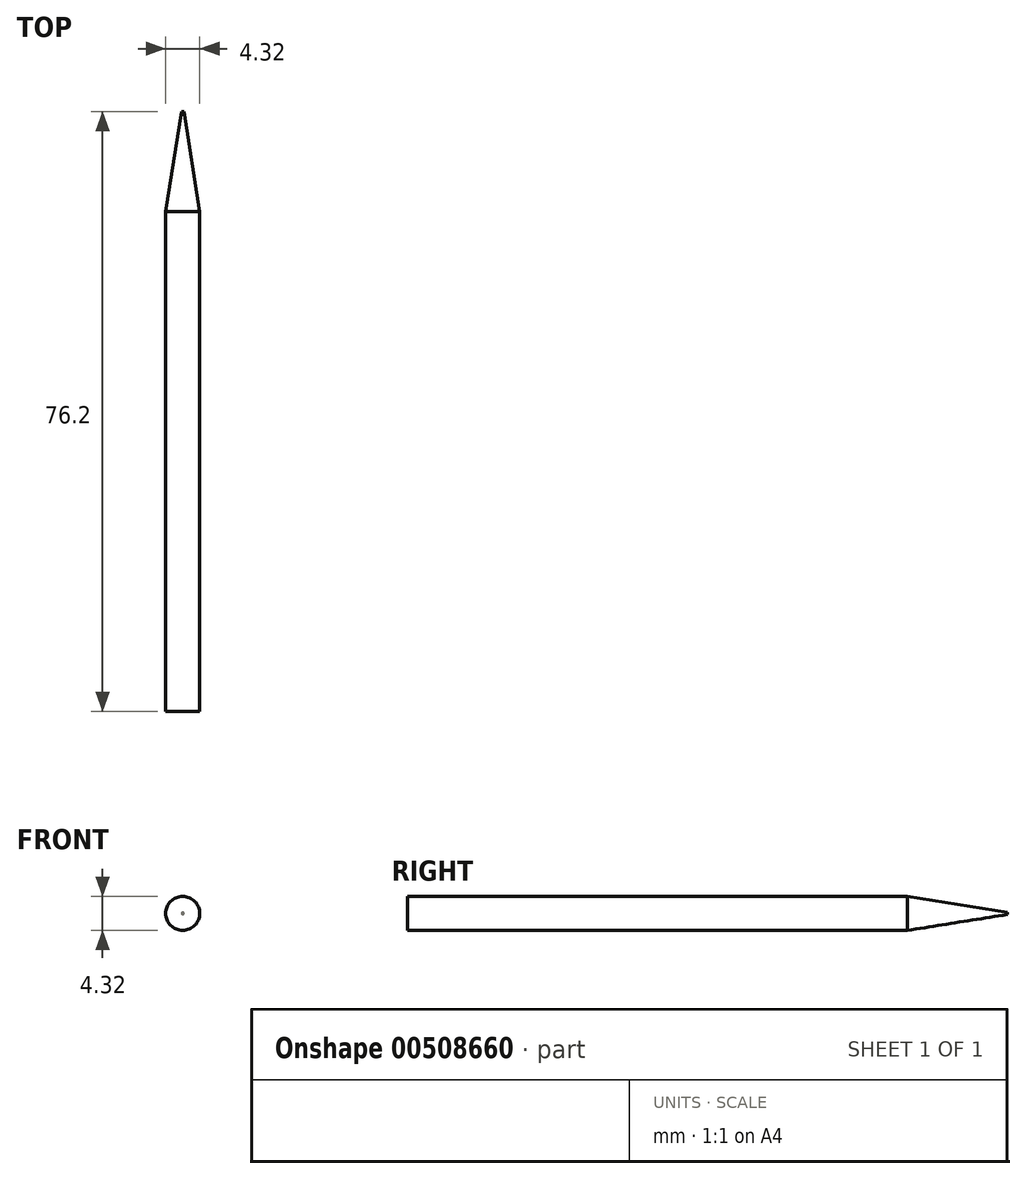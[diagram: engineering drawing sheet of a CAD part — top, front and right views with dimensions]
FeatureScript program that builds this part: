
annotation { "Feature Type Name" : "Feature", "Feature Type Description" : "" }
export const myFeature = defineFeature(function(context is Context, id is Id, definition is map)
    precondition{}
    {
        {
            var Q0;
            Q0=qCreatedBy(makeId("Front.planeOp"),FACE);
            var sketch = newSketch(context, id + "F0", { "sketchPlane" : qUnion([Q0])});
            skCircle(sketch, "E0", {"center": v(0, 0) * mm, "radius": 2.16 * mm});
            skSolve(sketch);
        }
        {
            var Q0;
            Q0 = qSketchRegion(id + "F0", true);
            extrude(context, id + "F1", {"entities" : qUnion([Q0]), "depth" : 76.2 * mm});
        }
        {
            var Q0;
            Q0=makeQuery(id+"F1.opExtrude","CAP_EDGE",EDGE,{"disambiguationData":[OSD([sQuery(id+"F0.wireOp",EDGE,"E0")])],"isStart":true});
            chamfer(context, id + "F2", {"entities" : qUnion([Q0]), "chamferType" : ChamferType.OFFSET_ANGLE, "width" : 12.7 * mm, "oppositeDirection" : false, "angle" : 9 * degree});
        }
    });
